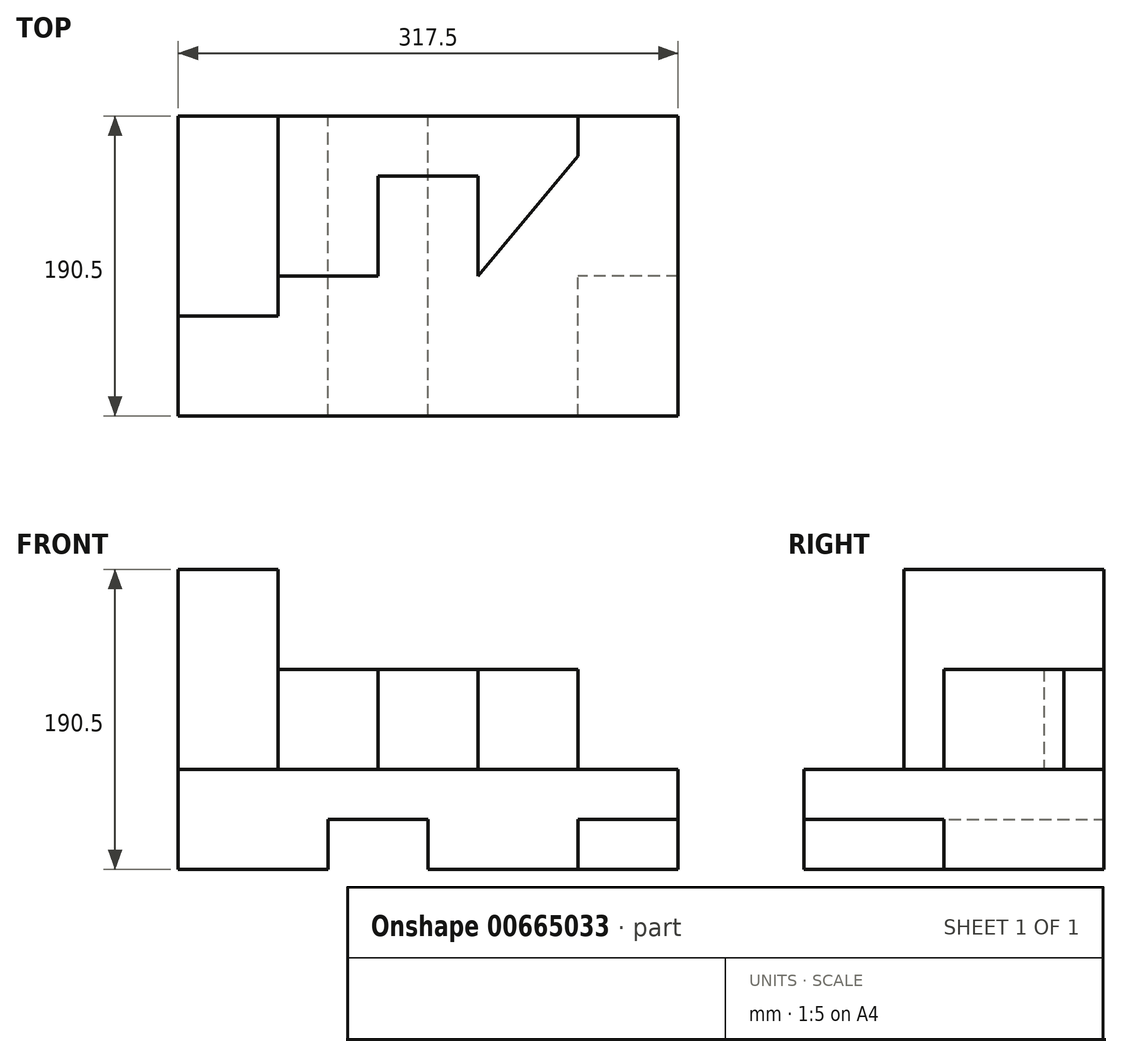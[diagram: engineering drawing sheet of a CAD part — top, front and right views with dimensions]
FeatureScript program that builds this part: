
annotation { "Feature Type Name" : "Feature", "Feature Type Description" : "" }
export const myFeature = defineFeature(function(context is Context, id is Id, definition is map)
    precondition{}
    {
        {
            var Q0;
            Q0=qCreatedBy(makeId("Front.planeOp"),FACE);
            var sketch = newSketch(context, id + "F0", { "sketchPlane" : qUnion([Q0])});
            skLineSegment(sketch, "E0", {"start": v(0, 0) * mm, "end": v(0, 63.5) * mm});
            skLineSegment(sketch, "E1", {"start": v(0, 63.5) * mm, "end": v(317.5, 63.5) * mm});
            skLineSegment(sketch, "E2", {"start": v(317.5, 63.5) * mm, "end": v(317.5, 31.75) * mm});
            skLineSegment(sketch, "E3", {"start": v(317.5, 31.75) * mm, "end": v(254, 31.75) * mm});
            skLineSegment(sketch, "E4", {"start": v(254, 31.75) * mm, "end": v(254, 0) * mm});
            skLineSegment(sketch, "E5", {"start": v(254, 0) * mm, "end": v(158.75, 0) * mm});
            skLineSegment(sketch, "E6", {"start": v(158.75, 0) * mm, "end": v(158.75, 31.75) * mm});
            skLineSegment(sketch, "E7", {"start": v(158.75, 31.75) * mm, "end": v(95.25, 31.75) * mm});
            skLineSegment(sketch, "E8", {"start": v(95.25, 31.75) * mm, "end": v(95.25, 0) * mm});
            skLineSegment(sketch, "E9", {"start": v(95.25, 0) * mm, "end": v(0, 0) * mm});
            skSolve(sketch);
        }
        {
            var Q0;
            Q0=makeQuery(id+"F0.imprint","IMPRINT",FACE,{"disambiguationData":[TD([[makeQuery(id+"F0.imprint","IMPRINT",EDGE,{"derivedFrom":sQuery(id+"F0.wireOp",EDGE,"E0")}),-1.0]])]});
            extrude(context, id + "F1", {"entities" : qUnion([Q0]), "endBound" : BoundingType.SYMMETRIC, "depth" : 190.5 * mm, "offsetDistance" : 25.4 * mm});
        }
        {
            var Q0;
            Q0=makeQuery(id+"F1.opExtrude","SWEPT_FACE",FACE,{"disambiguationData":[OSD([sQuery(id+"F0.wireOp",EDGE,"E4")])]});
            var sketch = newSketch(context, id + "F2", { "sketchPlane" : qUnion([Q0])});
            skLineSegment(sketch, "E10.0", {"start": v(-6.35, 31.75) * mm, "end": v(-6.35, 0) * mm});
            skSolve(sketch);
        }
        {
            var Q0;
            {var subQ0=sQuery(id+"F2.wireOp",EDGE,"E10.0");Q0=makeQuery(id+"F2.imprint","IMPRINT",FACE,{"disambiguationData":[TD([[makeQuery(id+"F2.imprint","IMPRINT",EDGE,{"derivedFrom":subQ0}),1.0]])]});}
            extrude(context, id + "F3", {"entities" : qUnion([Q0]), "operationType" : NewBodyOperationType.ADD, "endBound" : BoundingType.SYMMETRIC, "depth" : 127 * mm, "offsetDistance" : 25.4 * mm});
        }
        {
            var Q0;
            Q0=makeQuery(id+"F1.opExtrude","CAP_FACE",FACE,{"disambiguationData":[OSD([sQuery(id+"F0.wireOp",EDGE,"E0"),sQuery(id+"F0.wireOp",EDGE,"E1"),sQuery(id+"F0.wireOp",EDGE,"E2"),sQuery(id+"F0.wireOp",EDGE,"E3"),sQuery(id+"F0.wireOp",EDGE,"E4"),sQuery(id+"F0.wireOp",EDGE,"E5"),sQuery(id+"F0.wireOp",EDGE,"E6"),sQuery(id+"F0.wireOp",EDGE,"E7"),sQuery(id+"F0.wireOp",EDGE,"E8"),sQuery(id+"F0.wireOp",EDGE,"E9")])],"isStart":false});
            var sketch = newSketch(context, id + "F4", { "sketchPlane" : qUnion([Q0])});
            skLineSegment(sketch, "E11", {"start": v(0, 63.5) * mm, "end": v(0, 190.5) * mm});
            skLineSegment(sketch, "E12", {"start": v(0, 190.5) * mm, "end": v(63.5, 190.5) * mm});
            skLineSegment(sketch, "E13", {"start": v(63.5, 190.5) * mm, "end": v(63.5, 63.5) * mm});
            skSolve(sketch);
        }
        {
            var Q0;
            {var subQ0=sQuery(id+"F4.wireOp",EDGE,"E11");Q0=makeQuery(id+"F4.imprint","IMPRINT",FACE,{"disambiguationData":[TD([[makeQuery(id+"F4.imprint","IMPRINT",EDGE,{"derivedFrom":subQ0}),-1.0]])]});}
            extrude(context, id + "F5", {"entities" : qUnion([Q0]), "operationType" : NewBodyOperationType.ADD, "oppositeDirection" : true, "depth" : 190.5 * mm, "offsetDistance" : 25.4 * mm, "hasSecondDirection" : true, "secondDirectionOppositeDirection" : true, "secondDirectionDepth" : 63.5 * mm});
        }
        {
            var Q0;
            Q0=makeQuery(id+"F1.opExtrude","SWEPT_FACE",FACE,{"disambiguationData":[OSD([sQuery(id+"F0.wireOp",EDGE,"E1")])]});
            var sketch = newSketch(context, id + "F6", { "sketchPlane" : qUnion([Q0])});
            skLineSegment(sketch, "E14.0", {"start": v(63.5, -6.35) * mm, "end": v(127, -6.35) * mm});
            skLineSegment(sketch, "E15", {"start": v(127, -6.35) * mm, "end": v(127, 57.15) * mm});
            skLineSegment(sketch, "E16", {"start": v(127, 57.15) * mm, "end": v(190.5, 57.15) * mm});
            skLineSegment(sketch, "E17", {"start": v(190.5, 57.15) * mm, "end": v(190.5, -6.35) * mm});
            skPoint(sketch, "E18.orphan", {"position": v(317.5, -6.35) * mm});
            skLineSegment(sketch, "E19", {"start": v(317.5, 95.25) * mm, "end": v(254, 95.25) * mm});
            skLineSegment(sketch, "E20", {"start": v(254, 95.25) * mm, "end": v(254, 69.85) * mm});
            skLineSegment(sketch, "E21", {"start": v(254, 69.85) * mm, "end": v(190.5, -6.35) * mm});
            skSolve(sketch);
        }
        {
            var Q0;
            {var subQ4=sQuery(id+"F6.wireOp",EDGE,"E14.0");Q0=makeQuery(id+"F6.imprint","IMPRINT",FACE,{"disambiguationData":[TD([[makeQuery(id+"F6.imprint","IMPRINT",EDGE,{"derivedFrom":subQ4}),1.0]])]});}
            extrude(context, id + "F7", {"entities" : qUnion([Q0]), "operationType" : NewBodyOperationType.ADD, "depth" : 63.5 * mm, "offsetDistance" : 25.4 * mm});
        }
    });
